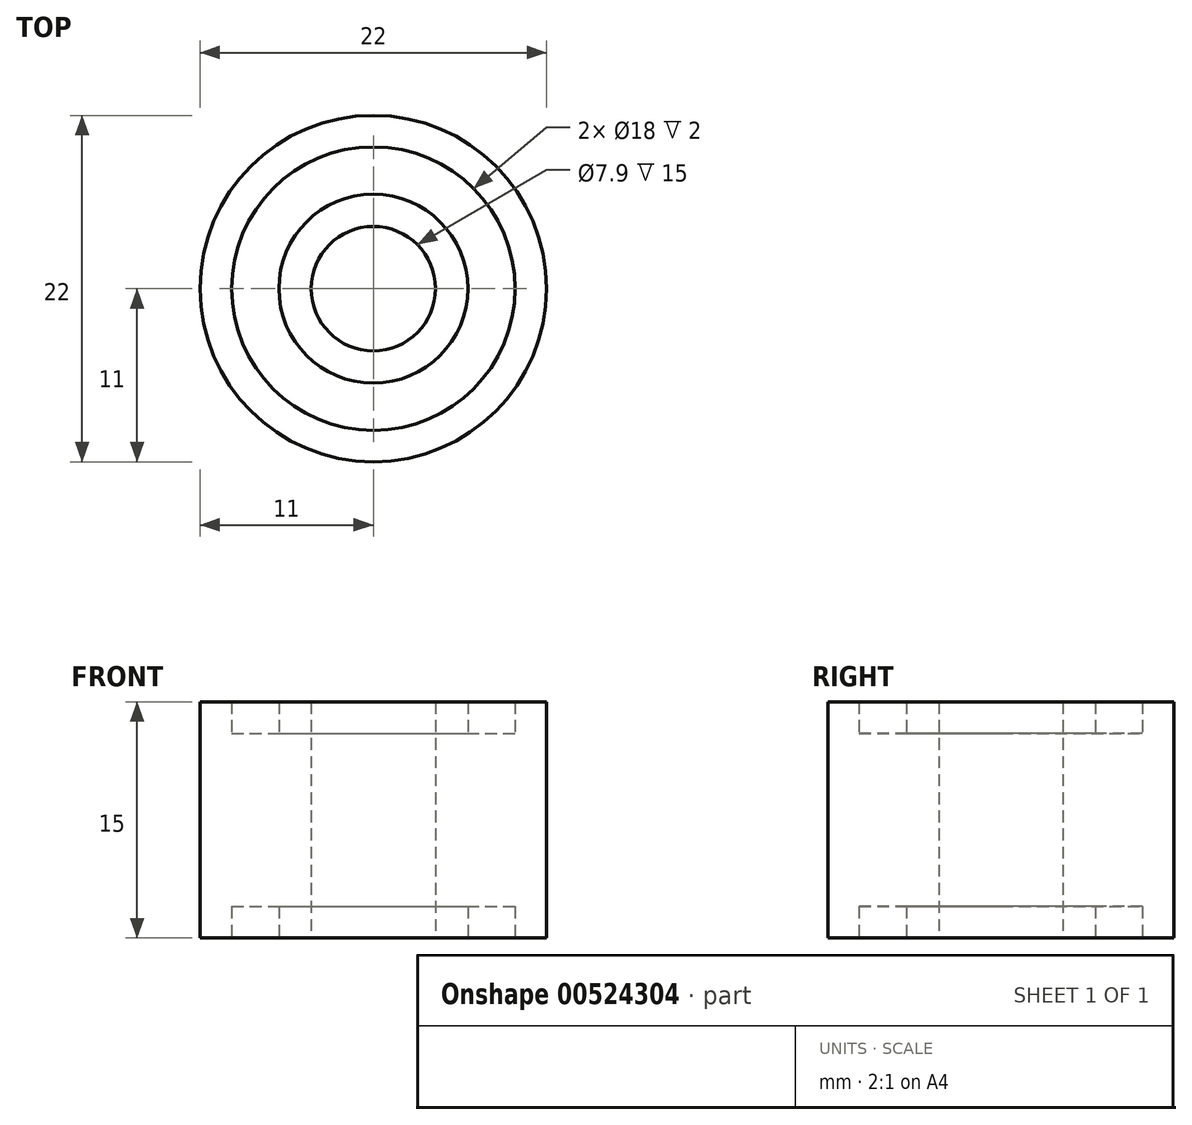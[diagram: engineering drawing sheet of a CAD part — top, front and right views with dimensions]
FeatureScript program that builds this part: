
annotation { "Feature Type Name" : "Feature", "Feature Type Description" : "" }
export const myFeature = defineFeature(function(context is Context, id is Id, definition is map)
    precondition{}
    {
        {
            var Q0;
            Q0=qCreatedBy(makeId("Front.planeOp"),FACE);
            var sketch = newSketch(context, id + "F0", { "sketchPlane" : qUnion([Q0])});
            skLineSegment(sketch, "E0.bottom", {"start": v(-3.95, 0) * mm, "end": v(-6, 0) * mm});
            skLineSegment(sketch, "E0.top", {"start": v(-3.95, 15) * mm, "end": v(-6, 15) * mm});
            skLineSegment(sketch, "E0.left", {"start": v(0, 0) * mm, "end": v(0, 15) * mm, "construction": true});
            skLineSegment(sketch, "E0.right", {"start": v(-11, 0) * mm, "end": v(-11, 15) * mm});
            skLineSegment(sketch, "E1.left", {"start": v(-3.95, 15) * mm, "end": v(-3.95, 10.23) * mm});
            skLineSegment(sketch, "E1.right", {"start": v(-6, 15) * mm, "end": v(-6, 10.23) * mm});
            skLineSegment(sketch, "E2.top", {"start": v(-6, 13) * mm, "end": v(-9, 13) * mm});
            skLineSegment(sketch, "E2.left", {"start": v(-6, 15) * mm, "end": v(-6, 13) * mm});
            skLineSegment(sketch, "E2.right", {"start": v(-9, 15) * mm, "end": v(-9, 13) * mm});
            skLineSegment(sketch, "E3", {"start": v(-3.95, 10.23) * mm, "end": v(-3.95, 0) * mm});
            skLineSegment(sketch, "E4", {"start": v(-9, 0) * mm, "end": v(-9, 2) * mm});
            skLineSegment(sketch, "E5", {"start": v(-9, 2) * mm, "end": v(-6, 2) * mm});
            skLineSegment(sketch, "E6", {"start": v(-6, 2) * mm, "end": v(-6, 0) * mm});
            skLineSegment(sketch, "E7.trimOffspring", {"start": v(-9, 0) * mm, "end": v(-11, 0) * mm});
            skLineSegment(sketch, "E8.trimOffspring", {"start": v(-9, 15) * mm, "end": v(-11, 15) * mm});
            skPoint(sketch, "E9.orphan", {"position": v(-3.95, 2) * mm});
            skSolve(sketch);
        }
        {
            var Q0;
            Q0=makeQuery(id+"F0.imprint","IMPRINT",FACE,{"disambiguationData":[TD([[makeQuery(id+"F0.imprint","IMPRINT",EDGE,{"derivedFrom":sQuery(id+"F0.wireOp",EDGE,"E0.right")}),-1.0]])]});
            var Q1;
            Q1=sQuery(id+"F0.wireOp",EDGE,"E0.left");
            revolve(context, id + "F1", {"entities" : qUnion([Q0]), "axis" : qUnion([Q1]), "revolveType" : RevolveType.FULL});
        }
    });
